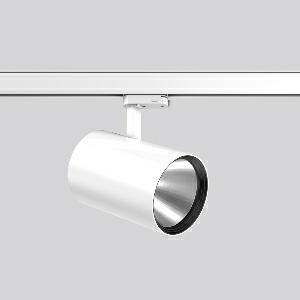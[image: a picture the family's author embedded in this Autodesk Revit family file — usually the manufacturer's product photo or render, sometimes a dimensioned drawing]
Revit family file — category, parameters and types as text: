
# Revit family: deecos_s_maxi_742216_002_3_eb41
name_source: partatom
category: Lighting Fixtures
units: mm (PartAtom-declared; Revit-internal decimal feet)

## family parameters
Cut with Voids When Loaded = No
Host = Face
Light Source = No
Part Type = Normal
Room Calculation Point = No
Round Connector Dimension = Use Diameter
Shared = No

## types (1)
- DEECOS S maxi (1 x LED Modul 935, 3250 lm, 3500)
    Apparent Load = 25 VA
    Approval mark = CE
    CIE Flux Codes = 97 100 100 100 100
    Color Rendering = 92
    Color Temperature = 3500
    Default Elevation = 1800 mm
    Description = Series: DEECOS S maxi
LED surface-mounted projector in modern design with no visible cooling ribs. Housing: die-cast aluminium, powder-coated. Rotation range: 356°. Swivel range: 90°. Black plastic ring and recessed LED to prevent glare from the side. Optical assembly with reflector made of MIRO-Silver with 98% total light reflection for outstanding efficiency - can be changed without tools. Best colour rendering index Ra>90. With multi adaptor for 3-circuit tracks 230 V. Suitable for Track on ceiling, Wall track. High quality converter without flickering and stroboscopic effect. The following accessories can be mounted without use of tools: interchangeable lenses, decorative glasses, honeycomb louvre, clear and frosted diffusers, white interchangeable plastic ring. 
Colour: traffic white, matt (RAL 9016)
Diameter: 123 mm
Height: 200 mm
Lamp: LED
Socket: without socket
Colour temperature: 3500K
Colour rendering index (CRI): 92
System power: 25 W
Rated luminous flux: 3250 lm
Luminous efficiency: 130 lm/W
Control gear: Regulated power supply
Protection class: I
Type of protection: IP 20
    Height = 200 mm  [stored 0.656168 ft]
    Lamp = 1 x LED Modul 935
    Lamp Light Flux = 3250 lm
    Lamp count = 1
    Length = 123 mm
    Lifetime = 50000 h
    Luminous efficacy = 130 lm/W
    Manufacturer = RZB
    ModVariant = No
    Model = 742216.002.3
    Mounting Place = Ceiling
    Mounting Type = Rail mounted
    Number of Poles = 1
    OnlyDefault = Yes
    Power Factor = 1
    Product Name = DEECOS S maxi
    Product group = Track mounted projectors
    ProductGroupID = 301
    Protection Class = Protection class I
    Protection Degree = IP 20
    RLX_Detail_Level = 1
    RLX_Emergency_Light_Flux = 0 lm
    RLX_Emergency_Type = 0
    RLX_Emergency_Type_DB = No
    RlxData = <blob elided: 38797 chars, md5=7d17e05f>
    Socket = socket
    Standby Power = 0 W
    System Light Flux = 3250 lm
    System Power = 25 W
    Type Comments = Product without accessories
    Type Image = 741954.002.jpg
    URL = http://relux.com
    VarID = ---
    Voltage = 230 V
    Voltage Range = 220-240 V
    Weight = 0.00 kg
    Width = 0 mm  [stored 0 ft]

note: [stored X ft] marks values corroborated as IEEE doubles in the binary element streams (Revit-internal decimal feet)

## geometry (parser evidence)
native form markers: Blend x4, Sweep x12
no freeform markers — native parametric forms only
